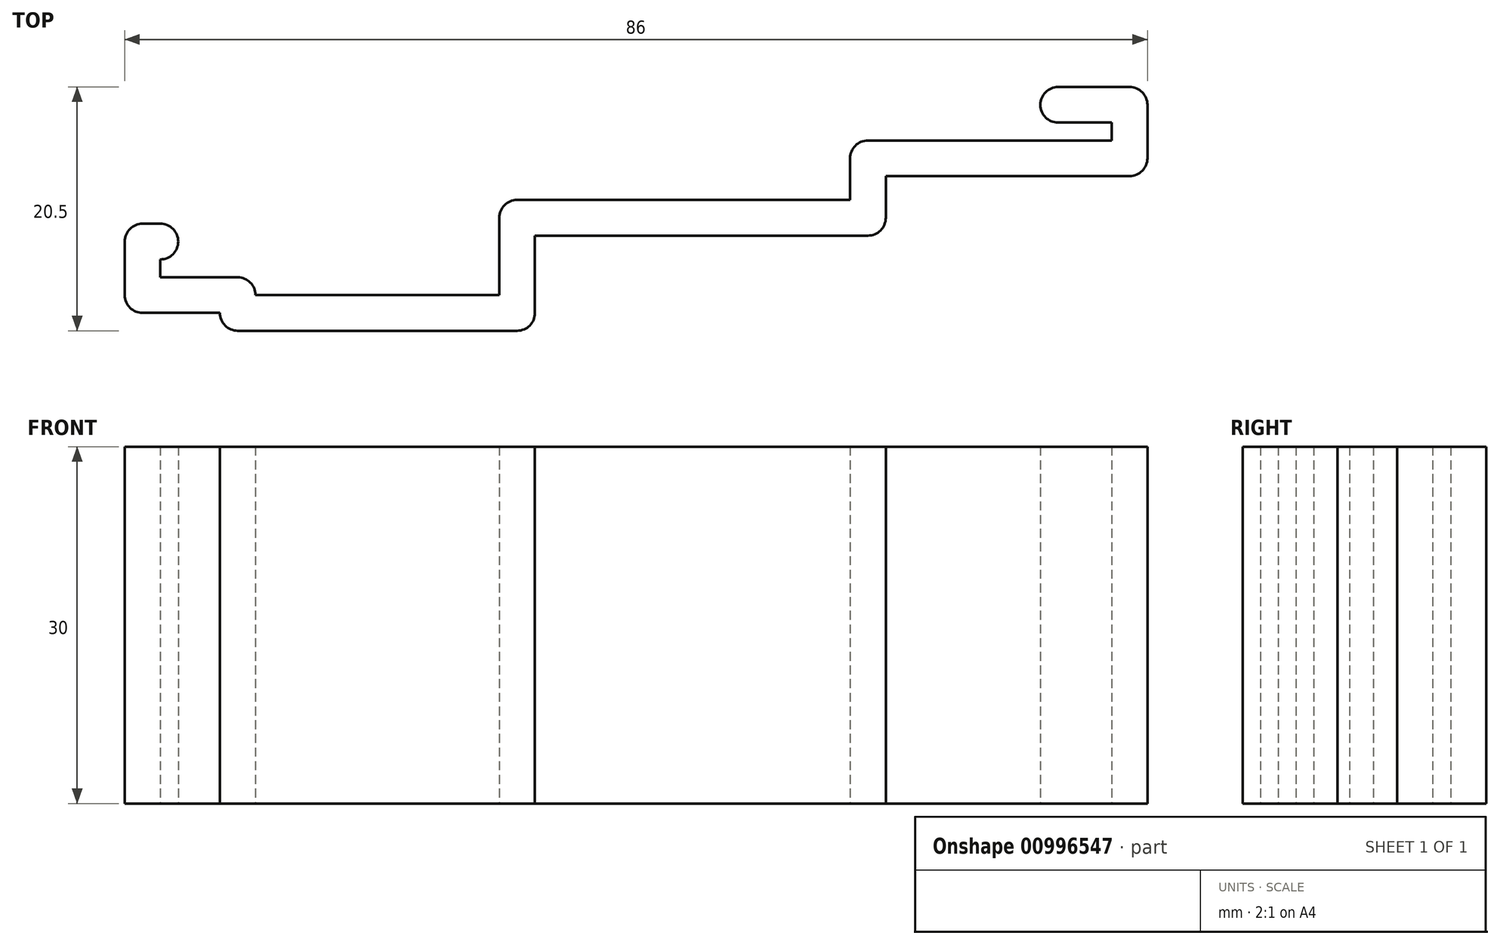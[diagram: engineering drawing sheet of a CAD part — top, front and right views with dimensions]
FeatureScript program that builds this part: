
annotation { "Feature Type Name" : "Feature", "Feature Type Description" : "" }
export const myFeature = defineFeature(function(context is Context, id is Id, definition is map)
    precondition{}
    {
        {
            var Q0;
            Q0=qCreatedBy(makeId("Top.planeOp"),FACE);
            var sketch = newSketch(context, id + "F0", { "sketchPlane" : qUnion([Q0])});
            skLineSegment(sketch, "E0", {"start": v(0, 0) * mm, "end": v(-20.5, 0) * mm});
            skLineSegment(sketch, "E1", {"start": v(-20.5, 0) * mm, "end": v(-20.5, 1.5) * mm});
            skLineSegment(sketch, "E2", {"start": v(-20.5, 1.5) * mm, "end": v(-28.5, 1.5) * mm});
            skLineSegment(sketch, "E3", {"start": v(-28.5, 1.5) * mm, "end": v(-28.5, 3) * mm});
            skLineSegment(sketch, "E4", {"start": v(-28.5, 3) * mm, "end": v(-27, 3) * mm});
            skLineSegment(sketch, "E5", {"start": v(-27, 3) * mm, "end": v(-27, 6) * mm});
            skLineSegment(sketch, "E6", {"start": v(-27, 6) * mm, "end": v(-31.5, 6) * mm});
            skLineSegment(sketch, "E7", {"start": v(-31.5, 6) * mm, "end": v(-31.5, -1.5) * mm});
            skLineSegment(sketch, "E8", {"start": v(-31.5, -1.5) * mm, "end": v(-23.5, -1.5) * mm});
            skLineSegment(sketch, "E9", {"start": v(-23.5, -1.5) * mm, "end": v(-23.5, -3) * mm});
            skLineSegment(sketch, "E10", {"start": v(-23.5, -3) * mm, "end": v(3, -3) * mm});
            skLineSegment(sketch, "E11", {"start": v(3, -3) * mm, "end": v(3, 5) * mm});
            skLineSegment(sketch, "E12", {"start": v(0, 0) * mm, "end": v(0, 8) * mm});
            skLineSegment(sketch, "E13", {"start": v(0, 8) * mm, "end": v(29.5, 8) * mm});
            skLineSegment(sketch, "E14", {"start": v(29.5, 8) * mm, "end": v(29.5, 13) * mm});
            skLineSegment(sketch, "E15", {"start": v(29.5, 13) * mm, "end": v(51.5, 13) * mm});
            skLineSegment(sketch, "E16", {"start": v(51.5, 13) * mm, "end": v(51.5, 14.5) * mm});
            skLineSegment(sketch, "E17", {"start": v(51.5, 14.5) * mm, "end": v(45.5, 14.5) * mm});
            skLineSegment(sketch, "E18", {"start": v(45.5, 14.5) * mm, "end": v(45.5, 17.5) * mm});
            skLineSegment(sketch, "E19", {"start": v(45.5, 17.5) * mm, "end": v(54.5, 17.5) * mm});
            skLineSegment(sketch, "E20", {"start": v(54.5, 17.5) * mm, "end": v(54.5, 10) * mm});
            skLineSegment(sketch, "E21", {"start": v(54.5, 10) * mm, "end": v(32.5, 10) * mm});
            skLineSegment(sketch, "E22", {"start": v(32.5, 10) * mm, "end": v(32.5, 5) * mm});
            skLineSegment(sketch, "E23", {"start": v(32.5, 5) * mm, "end": v(3, 5) * mm});
            skSolve(sketch);
        }
        {
            var Q0;
            Q0=makeQuery(id+"F0.imprint","IMPRINT",FACE,{"disambiguationData":[TD([[makeQuery(id+"F0.imprint","IMPRINT",EDGE,{"derivedFrom":sQuery(id+"F0.wireOp",EDGE,"E0")}),1.0]])]});
            extrude(context, id + "F1", {"entities" : qUnion([Q0]), "depth" : 30 * mm, "offsetDistance" : 25 * mm});
        }
        {
            var Q0;
            Q0=makeQuery(id+"F1.opExtrude","SWEPT_EDGE",EDGE,{"disambiguationData":[OSD([sQuery(id+"F0.wireOp",EDGE,"E9"),sQuery(id+"F0.wireOp",EDGE,"E10")])]});
            var Q1;
            Q1=makeQuery(id+"F1.opExtrude","SWEPT_EDGE",EDGE,{"disambiguationData":[OSD([sQuery(id+"F0.wireOp",EDGE,"E7"),sQuery(id+"F0.wireOp",EDGE,"E8")])]});
            var Q2;
            Q2=makeQuery(id+"F1.opExtrude","SWEPT_EDGE",EDGE,{"disambiguationData":[OSD([sQuery(id+"F0.wireOp",EDGE,"E1"),sQuery(id+"F0.wireOp",EDGE,"E2")])]});
            var Q3;
            Q3=makeQuery(id+"F1.opExtrude","SWEPT_EDGE",EDGE,{"disambiguationData":[OSD([sQuery(id+"F0.wireOp",EDGE,"E5"),sQuery(id+"F0.wireOp",EDGE,"E6")])]});
            var Q4;
            Q4=makeQuery(id+"F1.opExtrude","SWEPT_EDGE",EDGE,{"disambiguationData":[OSD([sQuery(id+"F0.wireOp",EDGE,"E4"),sQuery(id+"F0.wireOp",EDGE,"E5")])]});
            var Q5;
            Q5=makeQuery(id+"F1.opExtrude","SWEPT_EDGE",EDGE,{"disambiguationData":[OSD([sQuery(id+"F0.wireOp",EDGE,"E6"),sQuery(id+"F0.wireOp",EDGE,"E7")])]});
            var Q6;
            Q6=makeQuery(id+"F1.opExtrude","SWEPT_EDGE",EDGE,{"disambiguationData":[OSD([sQuery(id+"F0.wireOp",EDGE,"E10"),sQuery(id+"F0.wireOp",EDGE,"E11")])]});
            var Q7;
            Q7=makeQuery(id+"F1.opExtrude","SWEPT_EDGE",EDGE,{"disambiguationData":[OSD([sQuery(id+"F0.wireOp",EDGE,"E12"),sQuery(id+"F0.wireOp",EDGE,"E13")])]});
            var Q8;
            Q8=makeQuery(id+"F1.opExtrude","SWEPT_EDGE",EDGE,{"disambiguationData":[OSD([sQuery(id+"F0.wireOp",EDGE,"E22"),sQuery(id+"F0.wireOp",EDGE,"E23")])]});
            var Q9;
            Q9=makeQuery(id+"F1.opExtrude","SWEPT_EDGE",EDGE,{"disambiguationData":[OSD([sQuery(id+"F0.wireOp",EDGE,"E14"),sQuery(id+"F0.wireOp",EDGE,"E15")])]});
            var Q10;
            Q10=makeQuery(id+"F1.opExtrude","SWEPT_EDGE",EDGE,{"disambiguationData":[OSD([sQuery(id+"F0.wireOp",EDGE,"E18"),sQuery(id+"F0.wireOp",EDGE,"E19")])]});
            var Q11;
            Q11=makeQuery(id+"F1.opExtrude","SWEPT_EDGE",EDGE,{"disambiguationData":[OSD([sQuery(id+"F0.wireOp",EDGE,"E17"),sQuery(id+"F0.wireOp",EDGE,"E18")])]});
            var Q12;
            Q12=makeQuery(id+"F1.opExtrude","SWEPT_EDGE",EDGE,{"disambiguationData":[OSD([sQuery(id+"F0.wireOp",EDGE,"E20"),sQuery(id+"F0.wireOp",EDGE,"E21")])]});
            var Q13;
            Q13=makeQuery(id+"F1.opExtrude","SWEPT_EDGE",EDGE,{"disambiguationData":[OSD([sQuery(id+"F0.wireOp",EDGE,"E19"),sQuery(id+"F0.wireOp",EDGE,"E20")])]});
            fillet(context, id + "F2", {"entities" : qUnion([Q0, Q1, Q2, Q3, Q4, Q5, Q6, Q7, Q8, Q9, Q10, Q11, Q12, Q13]), "radius" : 1.5 * mm, "tangentPropagation" : true, "allowEdgeOverflow" : false});
        }
    });
